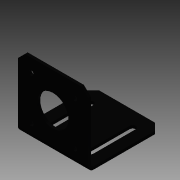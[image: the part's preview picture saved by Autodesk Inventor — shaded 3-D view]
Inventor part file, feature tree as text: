
AUTODESK INVENTOR PART (.ipt)
format: ipt  version: 2015 SP1 (Build 190203100, 203)  size: 144,384 bytes
history: native  units: mm
features: sheet_metal_op x2, other x2, plane x2, sketch x1
ambient origin geometry x8: Origin, YZ Plane, XZ Plane, XY Plane, X Axis, Y Axis, Z Axis, Center Point
bodies: Solid1 (feature_tree)
feature tree (7):
  sketch  "Sketch1"  dims[d0=31.0mm d1=50.0mm d2=100.0mm d4=22.1mm d5=49.0mm d6=31.0mm d7=3.5mm d8=30.0mm d9=4.2mm d10=30.0mm d11=11.0mm d12=9.5mm d13=9.5mm d14=31.0mm d15=2.0mm d16=2.0mm d17=1.0mm d18=4.0mm d19=2.0mm d20=90.0deg d21=2.0mm d22=5.0mm d23=6.0mm d24=45.0deg]
  sheet_metal_op  "Face1"
  sheet_metal_op  "Fold1"
  other  "Corner Chamfer1"
  plane  "Work Plane1"
  plane  "Work Plane2"
  other  "Plate1"
